# Revit family: 201_KNI-_
name_source: partatom
category: Air Terminals
units: mm (PartAtom-declared; Revit-internal decimal feet)

## family parameters
Always vertical = Yes
Cut with Voids When Loaded = No
Part Type = Normal
Room Calculation Point = Yes
Round Connector Dimension = Use Diameter
Shared = No
Work Plane-Based = No

## types (5) — shared parameters
B = 10 mm  [stored 0.0328084 ft]
B1 = 13 mm  [stored 0.0426509 ft]
B1__ve = -13 mm  [stored -0.0426509 ft]
B__ve = -10 mm  [stored -0.0328084 ft]
CL_Location_5000 = 5000 mm  [stored 16.4042 ft]
Description = AIR SUPPLY VALVE - INSULATED
L_ARR = 400 mm  [stored 1.31234 ft]
Manufacturer = Alnor
QmdConnectorList = 201;D
URL = http://www.ventilation-alnor.co.uk
W_ARR = 400 mm  [stored 1.31234 ft]
XRefLineVPlnId = 7453
YRefLineVPlnId = 7456
magiPartTypeId = 201
magiProductFamilyId = KNI-*
zero-valued in all types: CLBTZ, H_ARR

## per-type parameters (varying)
| type | A | B22 | D | R |
| KNI-080 | 115 mm  [stored 0.377297 ft] | 18 mm  [stored 0.0590551 ft] | 80 mm | 40 mm  [stored 0.131234 ft] |
| KNI-200 | 248 mm | 23 mm | 200 mm | 100 mm  [stored 0.328084 ft] |
| KNI-160 | 212 mm | 23 mm | 160 mm | 80 mm  [stored 0.262467 ft] |
| KNI-125 | 164 mm | 23 mm | 125 mm | 63 mm |
| KNI-100 | 137 mm | 18 mm  [stored 0.0590551 ft] | 100 mm | 50 mm |

note: column(s) folded — value = type name in every type: MC Product Code, magiProductId

note: [stored X ft] marks values corroborated as IEEE doubles in the binary element streams (Revit-internal decimal feet)

## geometry (parser evidence)
native form markers: Blend x2, Sweep x2
no freeform markers — native parametric forms only
